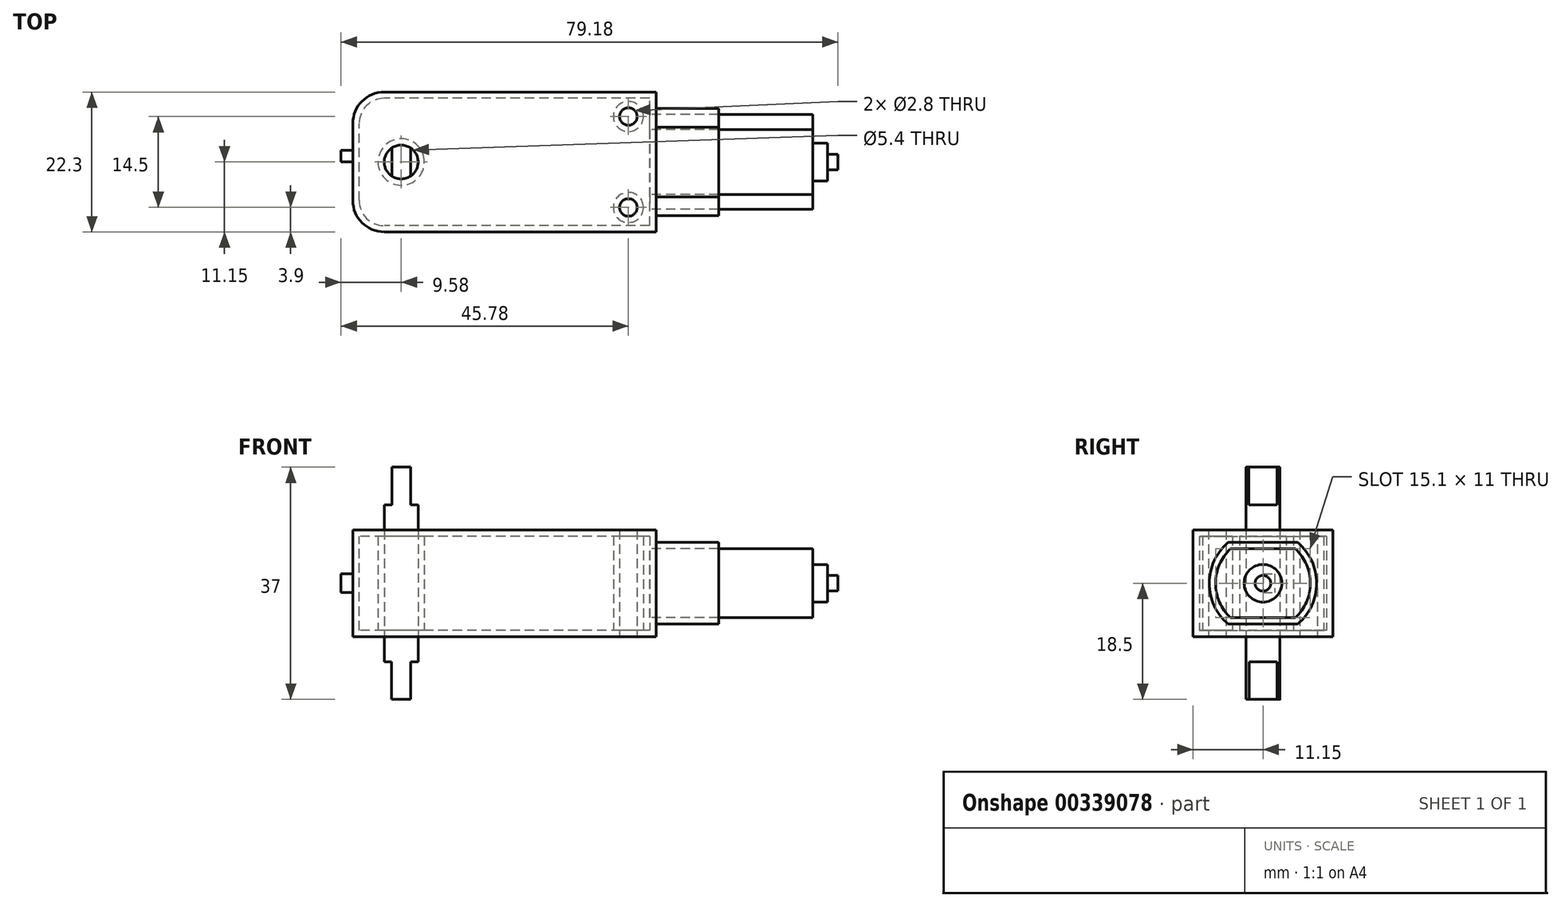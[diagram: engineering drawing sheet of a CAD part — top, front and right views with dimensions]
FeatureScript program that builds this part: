
annotation { "Feature Type Name" : "Feature", "Feature Type Description" : "" }
export const myFeature = defineFeature(function(context is Context, id is Id, definition is map)
    precondition{}
    {
        {
            var Q0;
            Q0=qCreatedBy(makeId("Top.planeOp"),FACE);
            var sketch = newSketch(context, id + "F0", { "sketchPlane" : qUnion([Q0])});
            skLineSegment(sketch, "E0.bottom", {"start": v(24.15, -11.15) * mm, "end": v(-19.15, -11.15) * mm});
            skLineSegment(sketch, "E0.top", {"start": v(24.15, 11.15) * mm, "end": v(-19.15, 11.15) * mm});
            skLineSegment(sketch, "E0.left", {"start": v(24.15, -11.15) * mm, "end": v(24.15, 11.15) * mm});
            skLineSegment(sketch, "E0.right", {"start": v(-24.15, -6.15) * mm, "end": v(-24.15, 6.15) * mm});
            skPoint(sketch, "E0.middle", {"position": v(0, 0) * mm});
            skLineSegment(sketch, "E1", {"start": v(16.16, 11.15) * mm, "end": v(16.16, -11.15) * mm});
            skCircle(sketch, "E2", {"center": v(19.75, 7.25) * mm, "radius": 1.4 * mm});
            skCircle(sketch, "E3", {"center": v(19.75, -7.25) * mm, "radius": 1.4 * mm});
            skCircle(sketch, "E4", {"center": v(-16.45, 0) * mm, "radius": 2.7 * mm});
            skLineSegment(sketch, "E5", {"start": v(-24.15, 1.88) * mm, "end": v(-26.03, 1.88) * mm});
            skLineSegment(sketch, "E6", {"start": v(-26.03, 1.88) * mm, "end": v(-26.03, 0) * mm});
            skLineSegment(sketch, "E7", {"start": v(-26.03, 0) * mm, "end": v(-24.15, 0) * mm});
            skPoint(sketch, "E8.visualSharp", {"position": v(-24.15, 11.15) * mm});
            skArc(sketch, "E8.filletArc", {"start": v(-19.15, 11.15) * mm, "mid": v(-22.69, 9.69) * mm, "end": v(-24.15, 6.15) * mm});
            skPoint(sketch, "E9.visualSharp", {"position": v(-24.15, -11.15) * mm});
            skArc(sketch, "E9.filletArc", {"start": v(-24.15, -6.15) * mm, "mid": v(-22.69, -9.69) * mm, "end": v(-19.15, -11.15) * mm});
            skSolve(sketch);
        }
        {
            var Q0;
            {var subQ0=sQuery(id+"F0.wireOp",EDGE,"E0.left");Q0=makeQuery(id+"F0.imprint","IMPRINT",FACE,{"disambiguationData":[TD([[makeQuery(id+"F0.imprint","IMPRINT",EDGE,{"derivedFrom":subQ0}),1.0]])]});}
            var Q1;
            {var subQ1=sQuery(id+"F0.wireOp",EDGE,"E1");Q1=makeQuery(id+"F0.imprint","IMPRINT",FACE,{"disambiguationData":[TD([[makeQuery(id+"F0.imprint","IMPRINT",EDGE,{"derivedFrom":subQ1}),-1.0]])]});}
            extrude(context, id + "F1", {"entities" : qUnion([Q0, Q1]), "depth" : 17 * mm, "symmetric" : true});
        }
        {
            var Q0;
            {var subQ0=sQuery(id+"F0.wireOp",EDGE,"E5");Q0=makeQuery(id+"F0.imprint","IMPRINT",FACE,{"disambiguationData":[TD([[makeQuery(id+"F0.imprint","IMPRINT",EDGE,{"derivedFrom":subQ0}),1.0]])]});}
            extrude(context, id + "F2", {"entities" : qUnion([Q0]), "operationType" : NewBodyOperationType.ADD, "depth" : 3 * mm, "symmetric" : true});
        }
        {
            var Q0;
            Q0=makeQuery(id+"F0.imprint","IMPRINT",FACE,{"disambiguationData":[TD([[makeQuery(id+"F0.imprint","IMPRINT",EDGE,{"derivedFrom":sQuery(id+"F0.wireOp",EDGE,"E4")}),1.0]])]});
            extrude(context, id + "F3", {"entities" : qUnion([Q0]), "depth" : 37 * mm, "symmetric" : true});
        }
        {
            var Q0;
            Q0=makeQuery(id+"F1.opExtrude","SWEPT_FACE",FACE,{"disambiguationData":[OSD([sQuery(id+"F0.wireOp",EDGE,"E0.left")])]});
            var sketch = newSketch(context, id + "F4", { "sketchPlane" : qUnion([Q0])});
            skArc(sketch, "E10", {"start": v(-5.55, 6.5) * mm, "mid": v(-8.55, 0) * mm, "end": v(-5.55, -6.5) * mm});
            skLineSegment(sketch, "E11.bottom", {"start": v(5.55, -6.5) * mm, "end": v(-5.55, -6.5) * mm});
            skLineSegment(sketch, "E11.top", {"start": v(5.55, 6.5) * mm, "end": v(-5.55, 6.5) * mm});
            skPoint(sketch, "E11.left.end.orphan", {"position": v(10.32, 6.5) * mm});
            skPoint(sketch, "E12.orphan", {"position": v(11.23, -6.5) * mm});
            skPoint(sketch, "E11.right.start.orphan", {"position": v(-10.32, -6.5) * mm});
            skPoint(sketch, "E13.orphan", {"position": v(-11.23, 6.5) * mm});
            skArc(sketch, "E14.trimOffspring", {"start": v(5.55, -6.5) * mm, "mid": v(8.55, 0) * mm, "end": v(5.55, 6.5) * mm});
            skSolve(sketch);
        }
        {
            var Q0;
            Q0=makeQuery(id+"F4.imprint","IMPRINT",FACE,{"disambiguationData":[TD([[makeQuery(id+"F4.imprint","IMPRINT",EDGE,{"derivedFrom":sQuery(id+"F4.wireOp",EDGE,"E10")}),1.0]])]});
            extrude(context, id + "F5", {"entities" : qUnion([Q0]), "operationType" : NewBodyOperationType.ADD, "depth" : 10 * mm});
        }
        {
            var Q0;
            Q0=makeQuery(id+"F5.opExtrude","CAP_FACE",FACE,{"disambiguationData":[OSD([sQuery(id+"F4.wireOp",EDGE,"E10"),sQuery(id+"F4.wireOp",EDGE,"E11.bottom"),sQuery(id+"F4.wireOp",EDGE,"E11.top"),sQuery(id+"F4.wireOp",EDGE,"E14.trimOffspring")])],"isStart":false});
            shell(context, id + "F6", {"entities" : qUnion([Q0]), "thickness" : 1 * mm});
        }
        {
            var Q0;
            Q0=makeQuery(id+"F5.opExtrude","CAP_FACE",FACE,{"disambiguationData":[OSD([sQuery(id+"F4.wireOp",EDGE,"E10"),sQuery(id+"F4.wireOp",EDGE,"E11.bottom"),sQuery(id+"F4.wireOp",EDGE,"E11.top"),sQuery(id+"F4.wireOp",EDGE,"E14.trimOffspring")])],"isStart":false});
            var sketch = newSketch(context, id + "F7", { "sketchPlane" : qUnion([Q0])});
            skArc(sketch, "E15.0", {"start": v(-5.17, 5.5) * mm, "mid": v(-7.55, 0) * mm, "end": v(-5.17, -5.5) * mm});
            skLineSegment(sketch, "E15.1", {"start": v(5.17, 5.5) * mm, "end": v(-5.17, 5.5) * mm});
            skArc(sketch, "E15.2", {"start": v(5.17, -5.5) * mm, "mid": v(7.55, 0) * mm, "end": v(5.17, 5.5) * mm});
            skLineSegment(sketch, "E15.3", {"start": v(5.17, -5.5) * mm, "end": v(-5.17, -5.5) * mm});
            skSolve(sketch);
        }
        {
            var Q0;
            Q0 = qSketchRegion(id + "F7", true);
            extrude(context, id + "F8", {"entities" : qUnion([Q0]), "depth" : 15 * mm, "offsetDistance" : 25 * mm});
        }
        {
            var Q0;
            Q0=makeQuery(id+"F8.opExtrude","CAP_FACE",FACE,{"disambiguationData":[OSD([sQuery(id+"F7.wireOp",EDGE,"E15.0"),sQuery(id+"F7.wireOp",EDGE,"E15.1"),sQuery(id+"F7.wireOp",EDGE,"E15.2"),sQuery(id+"F7.wireOp",EDGE,"E15.3")])],"isStart":false});
            var sketch = newSketch(context, id + "F9", { "sketchPlane" : qUnion([Q0])});
            skCircle(sketch, "E16", {"center": v(0, 0) * mm, "radius": 3 * mm});
            skCircle(sketch, "E17", {"center": v(0, 0) * mm, "radius": 1.25 * mm});
            skSolve(sketch);
        }
        {
            var Q0;
            Q0=makeQuery(id+"F9.imprint","IMPRINT",FACE,{"disambiguationData":[TD([[makeQuery(id+"F9.imprint","IMPRINT",EDGE,{"derivedFrom":sQuery(id+"F9.wireOp",EDGE,"E16")}),1.0]])]});
            extrude(context, id + "F10", {"entities" : qUnion([Q0]), "operationType" : NewBodyOperationType.ADD, "depth" : 2.3 * mm});
        }
        {
            var Q0;
            Q0=makeQuery(id+"F10.boolean.opBoolean","SPLIT",FACE,{"disambiguationData":[TD([makeQuery(id+"F10.opExtrude","SWEPT_FACE",FACE,{"disambiguationData":[OSD([sQuery(id+"F9.wireOp",EDGE,"E17")])]})])],"derivedFrom":makeQuery(id+"F8.opExtrude","CAP_FACE",FACE,{"disambiguationData":[OSD([sQuery(id+"F7.wireOp",EDGE,"E15.0"),sQuery(id+"F7.wireOp",EDGE,"E15.1"),sQuery(id+"F7.wireOp",EDGE,"E15.2"),sQuery(id+"F7.wireOp",EDGE,"E15.3")])],"isStart":false})});
            extrude(context, id + "F11", {"entities" : qUnion([Q0]), "operationType" : NewBodyOperationType.ADD, "depth" : 4 * mm, "offsetDistance" : 25 * mm});
        }
        {
            var Q0;
            Q0=makeQuery(id+"F3.opExtrude","CAP_FACE",FACE,{"disambiguationData":[OSD([sQuery(id+"F0.wireOp",EDGE,"E4")])],"isStart":false});
            var sketch = newSketch(context, id + "F12", { "sketchPlane" : qUnion([Q0])});
            skLineSegment(sketch, "E18.bottom", {"start": v(-14.96, -2.25) * mm, "end": v(-17.94, -2.25) * mm});
            skLineSegment(sketch, "E18.top", {"start": v(-14.96, 2.25) * mm, "end": v(-17.94, 2.25) * mm});
            skLineSegment(sketch, "E18.left", {"start": v(-14.96, -2.25) * mm, "end": v(-14.96, 2.25) * mm});
            skLineSegment(sketch, "E18.right", {"start": v(-17.94, -2.25) * mm, "end": v(-17.94, 2.25) * mm});
            skPoint(sketch, "E18.middle", {"position": v(-16.45, 0) * mm});
            skSolve(sketch);
        }
        {
            var Q0;
            {var subQ0=sQuery(id+"F12.wireOp",EDGE,"E18.right");Q0=makeQuery(id+"F12.imprint","IMPRINT",FACE,{"disambiguationData":[TD([[makeQuery(id+"F12.imprint","IMPRINT",EDGE,{"derivedFrom":subQ0}),1.0]])]});}
            var Q1;
            {var subQ0=sQuery(id+"F12.wireOp",EDGE,"E18.left");Q1=makeQuery(id+"F12.imprint","IMPRINT",FACE,{"disambiguationData":[TD([[makeQuery(id+"F12.imprint","IMPRINT",EDGE,{"derivedFrom":subQ0}),-1.0]])]});}
            extrude(context, id + "F13", {"entities" : qUnion([Q0, Q1]), "operationType" : NewBodyOperationType.REMOVE, "oppositeDirection" : true, "depth" : 6 * mm});
        }
        {
            var Q0;
            Q0=makeQuery(id+"F3.opExtrude","CAP_FACE",FACE,{"disambiguationData":[OSD([sQuery(id+"F0.wireOp",EDGE,"E4")])],"isStart":true});
            var sketch = newSketch(context, id + "F14", { "sketchPlane" : qUnion([Q0])});
            skLineSegment(sketch, "E19.bottom", {"start": v(-14.92, 2.23) * mm, "end": v(-17.98, 2.23) * mm});
            skLineSegment(sketch, "E19.top", {"start": v(-14.92, -2.23) * mm, "end": v(-17.98, -2.23) * mm});
            skLineSegment(sketch, "E19.left", {"start": v(-14.92, 2.23) * mm, "end": v(-14.92, -2.23) * mm});
            skLineSegment(sketch, "E19.right", {"start": v(-17.98, 2.23) * mm, "end": v(-17.98, -2.23) * mm});
            skPoint(sketch, "E19.middle", {"position": v(-16.45, 0) * mm});
            skSolve(sketch);
        }
        {
            var Q0;
            {var subQ0=sQuery(id+"F14.wireOp",EDGE,"E19.right");Q0=makeQuery(id+"F14.imprint","IMPRINT",FACE,{"disambiguationData":[TD([[makeQuery(id+"F14.imprint","IMPRINT",EDGE,{"derivedFrom":subQ0}),-1.0]])]});}
            var Q1;
            {var subQ0=sQuery(id+"F14.wireOp",EDGE,"E19.left");Q1=makeQuery(id+"F14.imprint","IMPRINT",FACE,{"disambiguationData":[TD([[makeQuery(id+"F14.imprint","IMPRINT",EDGE,{"derivedFrom":subQ0}),1.0]])]});}
            extrude(context, id + "F15", {"entities" : qUnion([Q0, Q1]), "operationType" : NewBodyOperationType.REMOVE, "oppositeDirection" : true, "depth" : 6 * mm});
        }
    });
